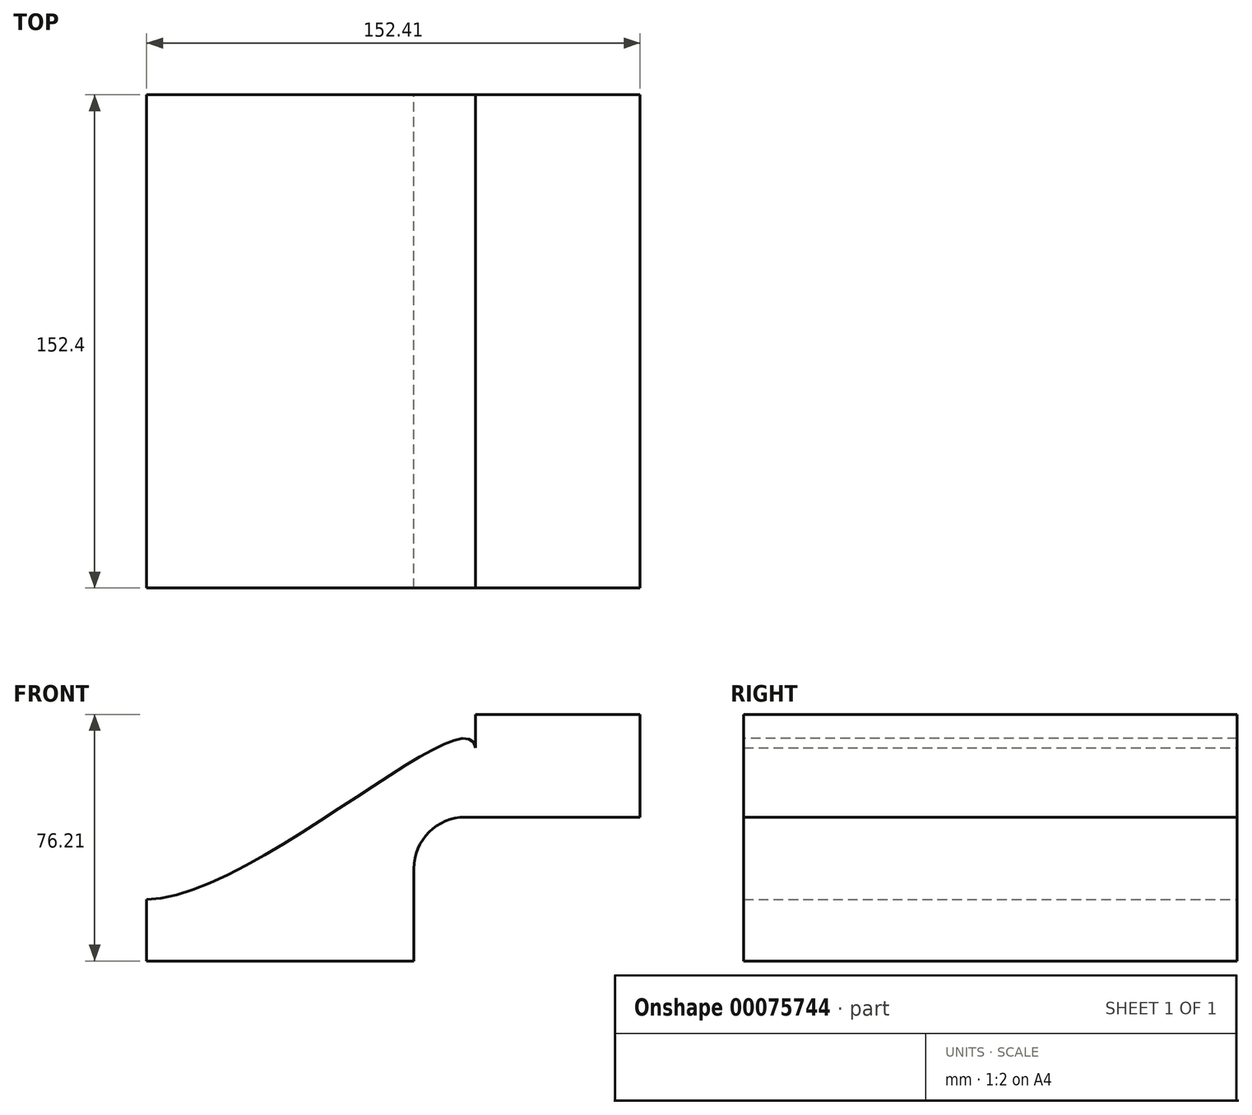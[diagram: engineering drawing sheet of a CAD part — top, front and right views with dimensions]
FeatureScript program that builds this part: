
annotation { "Feature Type Name" : "Feature", "Feature Type Description" : "" }
export const myFeature = defineFeature(function(context is Context, id is Id, definition is map)
    precondition{}
    {
        {
            var Q0;
            Q0=qCreatedBy(makeId("Front.planeOp"),FACE);
            var sketch = newSketch(context, id + "F0", { "sketchPlane" : qUnion([Q0])});
            skLineSegment(sketch, "E0.bottom", {"start": v(-41.27, -9.53) * mm, "end": v(41.28, -9.53) * mm});
            skLineSegment(sketch, "E0.top", {"start": v(-41.28, 9.53) * mm, "end": v(41.28, 9.53) * mm});
            skLineSegment(sketch, "E0.left", {"start": v(-41.28, -9.53) * mm, "end": v(-41.28, 9.52) * mm});
            skLineSegment(sketch, "E0.right", {"start": v(41.28, -9.53) * mm, "end": v(41.28, 9.52) * mm});
            skPoint(sketch, "E0.middle", {"position": v(0, 0) * mm});
            skLineSegment(sketch, "E1.bottom", {"start": v(111.13, 34.92) * mm, "end": v(60.33, 34.92) * mm});
            skLineSegment(sketch, "E1.top", {"start": v(111.13, 66.68) * mm, "end": v(60.33, 66.67) * mm});
            skLineSegment(sketch, "E1.left", {"start": v(111.13, 34.92) * mm, "end": v(111.13, 66.67) * mm});
            skLineSegment(sketch, "E1.right", {"start": v(60.33, 34.92) * mm, "end": v(60.33, 66.68) * mm});
            skPoint(sketch, "E1.middle", {"position": v(85.73, 50.8) * mm});
            skLineSegment(sketch, "E2", {"start": v(41.28, 9.52) * mm, "end": v(41.28, 19.05) * mm});
            skArc(sketch, "E3", {"start": v(41.28, 19.05) * mm, "mid": v(45.92, 30.28) * mm, "end": v(57.15, 34.93) * mm});
            skLineSegment(sketch, "E4", {"start": v(57.15, 34.92) * mm, "end": v(73.24, 34.92) * mm});
            skLineSegment(sketch, "E5.0", {"start": v(57.15, 53.97) * mm, "end": v(73.24, 53.97) * mm});
            skArc(sketch, "E5.1", {"start": v(22.23, 19.05) * mm, "mid": v(32.45, 43.75) * mm, "end": v(57.15, 53.98) * mm});
            skLineSegment(sketch, "E5.2", {"start": v(22.23, 9.52) * mm, "end": v(22.23, 19.05) * mm});
            skFitSpline(sketch, "E6", {"points": [v(-41.28, 9.52) * mm, v(60.33, 53.97) * mm], "startDerivative": vector(101.83, 0) * mm, "endDerivative": vector(-8.17, -73.53) * mm});
            skSolve(sketch);
        }
        {
            var Q0;
            Q0 = qSketchRegion(id + "F0", true);
            extrude(context, id + "F1", {"entities" : qUnion([Q0]), "depth" : 127 * mm});
        }
        {
            var Q0;
            Q0=makeQuery(id+"F1.opExtrude","CAP_FACE",FACE,{"disambiguationData":[OSD([sQuery(id+"F0.wireOp",EDGE,"E0.bottom"),sQuery(id+"F0.wireOp",EDGE,"E0.left"),sQuery(id+"F0.wireOp",EDGE,"E0.right"),sQuery(id+"F0.wireOp",EDGE,"E1.bottom"),sQuery(id+"F0.wireOp",EDGE,"E1.top"),sQuery(id+"F0.wireOp",EDGE,"E1.left"),sQuery(id+"F0.wireOp",EDGE,"E1.right"),sQuery(id+"F0.wireOp",EDGE,"E2"),sQuery(id+"F0.wireOp",EDGE,"E3"),sQuery(id+"F0.wireOp",EDGE,"E4"),sQuery(id+"F0.wireOp",EDGE,"E6")])],"isStart":false});
            var Q1;
            Q1=makeQuery(id+"F1.opExtrude","CAP_FACE",FACE,{"disambiguationData":[OSD([sQuery(id+"F0.wireOp",EDGE,"E0.bottom"),sQuery(id+"F0.wireOp",EDGE,"E0.left"),sQuery(id+"F0.wireOp",EDGE,"E0.right"),sQuery(id+"F0.wireOp",EDGE,"E1.bottom"),sQuery(id+"F0.wireOp",EDGE,"E1.top"),sQuery(id+"F0.wireOp",EDGE,"E1.left"),sQuery(id+"F0.wireOp",EDGE,"E1.right"),sQuery(id+"F0.wireOp",EDGE,"E2"),sQuery(id+"F0.wireOp",EDGE,"E3"),sQuery(id+"F0.wireOp",EDGE,"E4"),sQuery(id+"F0.wireOp",EDGE,"E6")])],"isStart":false});
            extrude(context, id + "F2", {"entities" : qUnion([Q0, Q1]), "operationType" : NewBodyOperationType.ADD, "depth" : 25.4 * mm});
        }
    });
